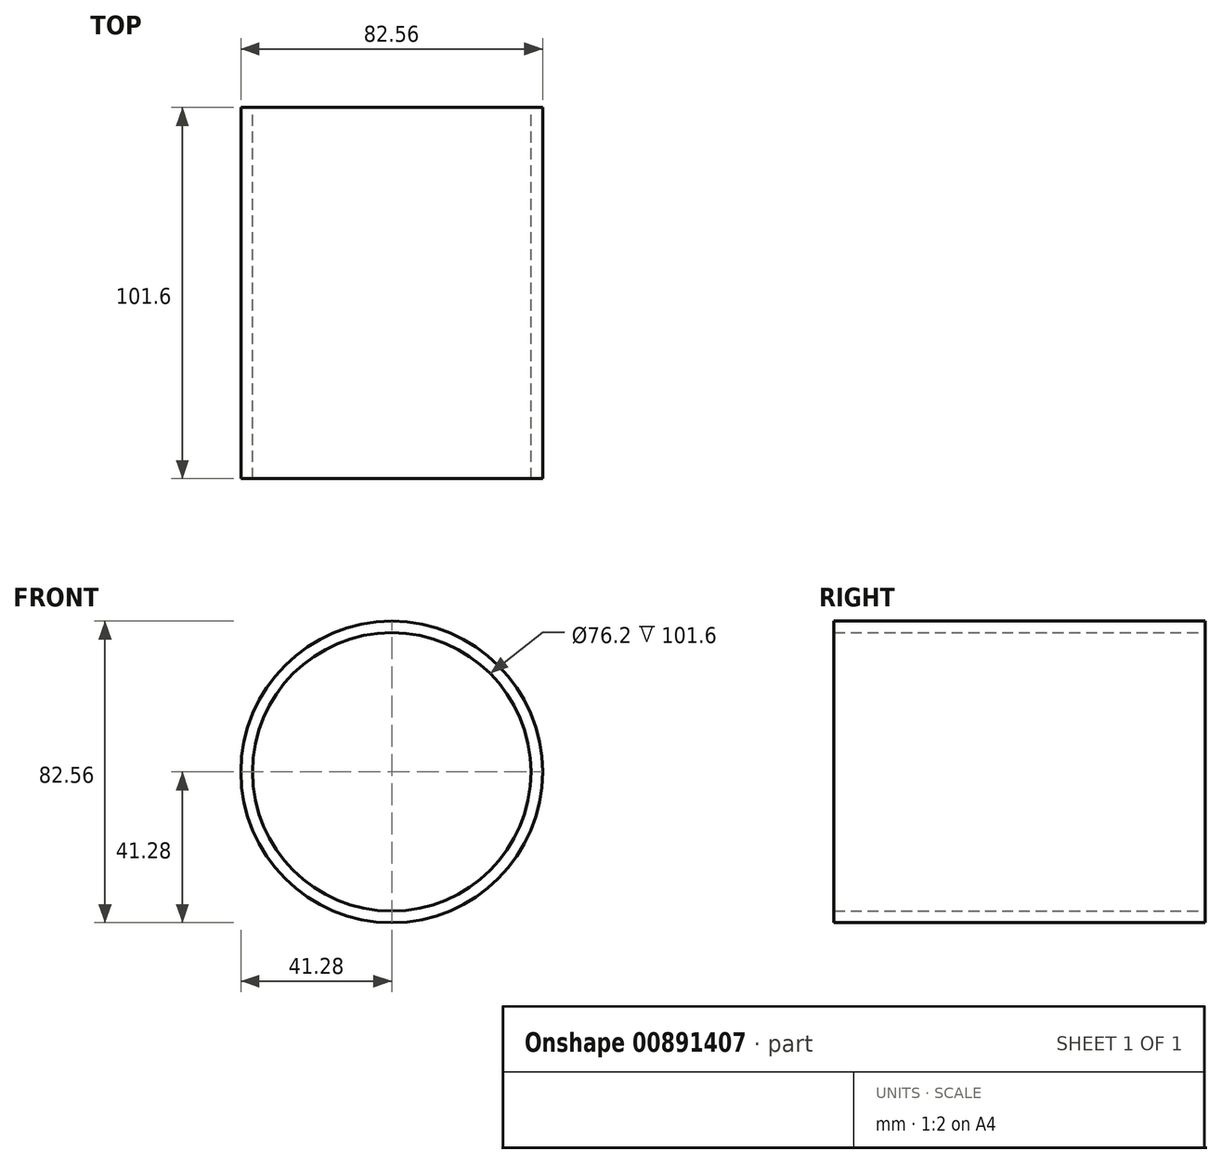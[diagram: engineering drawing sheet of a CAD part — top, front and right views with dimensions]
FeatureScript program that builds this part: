
annotation { "Feature Type Name" : "Feature", "Feature Type Description" : "" }
export const myFeature = defineFeature(function(context is Context, id is Id, definition is map)
    precondition{}
    {
        {
            var Q0;
            Q0=qCreatedBy(makeId("Front.planeOp"),FACE);
            var sketch = newSketch(context, id + "F0", { "sketchPlane" : qUnion([Q0])});
            skCircle(sketch, "E0", {"center": v(0, 0) * mm, "radius": 38.1 * mm});
            skLineSegment(sketch, "E1.bottom", {"start": v(28.57, -15.87) * mm, "end": v(-28.57, -15.88) * mm});
            skLineSegment(sketch, "E1.top", {"start": v(28.57, 15.88) * mm, "end": v(-28.57, 15.87) * mm});
            skLineSegment(sketch, "E1.left", {"start": v(28.57, -15.87) * mm, "end": v(28.57, 15.88) * mm});
            skLineSegment(sketch, "E1.right", {"start": v(-28.57, -15.88) * mm, "end": v(-28.57, 15.87) * mm});
            skCircle(sketch, "E2", {"center": v(0, 0) * mm, "radius": 41.28 * mm});
            skSolve(sketch);
        }
        {
            var Q0;
            Q0=makeQuery(id+"F0.imprint","IMPRINT",FACE,{"disambiguationData":[TD([[makeQuery(id+"F0.imprint","IMPRINT",EDGE,{"derivedFrom":sQuery(id+"F0.wireOp",EDGE,"E0")}),-1.0]])]});
            extrude(context, id + "F1", {"entities" : qUnion([Q0]), "depth" : 101.6 * mm, "offsetDistance" : 25.4 * mm});
        }
    });
